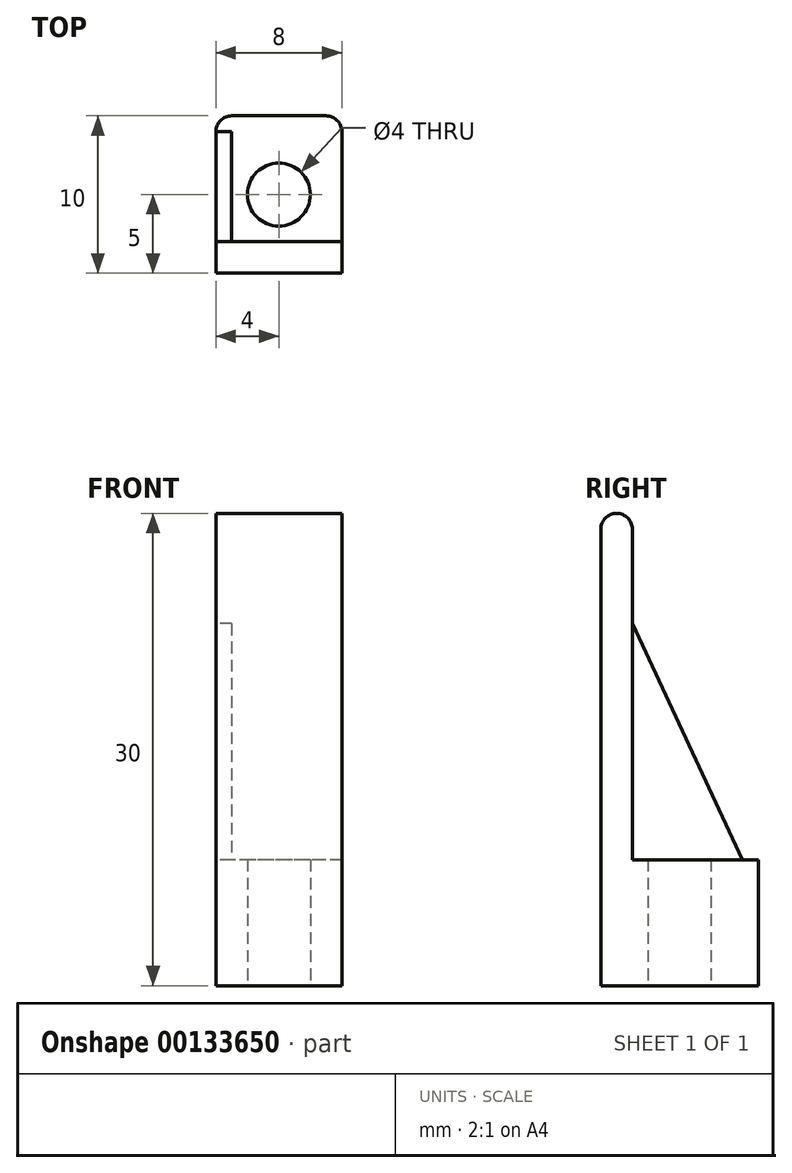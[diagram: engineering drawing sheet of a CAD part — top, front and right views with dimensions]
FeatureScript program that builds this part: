
annotation { "Feature Type Name" : "Feature", "Feature Type Description" : "" }
export const myFeature = defineFeature(function(context is Context, id is Id, definition is map)
    precondition{}
    {
        {
            var Q0;
            Q0=qCreatedBy(makeId("Top.planeOp"),FACE);
            var sketch = newSketch(context, id + "F0", { "sketchPlane" : qUnion([Q0])});
            skLineSegment(sketch, "E0.bottom", {"start": v(3, 5) * mm, "end": v(-3, 5) * mm});
            skLineSegment(sketch, "E0.top", {"start": v(4, -5) * mm, "end": v(-4, -5) * mm});
            skLineSegment(sketch, "E0.left", {"start": v(4, 4) * mm, "end": v(4, -5) * mm});
            skLineSegment(sketch, "E0.right", {"start": v(-4, 4) * mm, "end": v(-4, -5) * mm});
            skPoint(sketch, "E0.middle", {"position": v(0, 0) * mm});
            skCircle(sketch, "E1", {"center": v(0, 0) * mm, "radius": 2 * mm});
            skPoint(sketch, "E2.visualSharp", {"position": v(-4, 5) * mm});
            skArc(sketch, "E2.filletArc", {"start": v(-3, 5) * mm, "mid": v(-3.7, 4.7) * mm, "end": v(-4, 4) * mm});
            skPoint(sketch, "E3.visualSharp", {"position": v(4, 5) * mm});
            skArc(sketch, "E3.filletArc", {"start": v(4, 4) * mm, "mid": v(3.7, 4.7) * mm, "end": v(3, 5) * mm});
            skSolve(sketch);
        }
        {
            var Q0;
            Q0=makeQuery(id+"F0.imprint","IMPRINT",FACE,{"disambiguationData":[TD([[makeQuery(id+"F0.imprint","IMPRINT",EDGE,{"derivedFrom":sQuery(id+"F0.wireOp",EDGE,"E0.bottom")}),1.0]])]});
            extrude(context, id + "F1", {"entities" : qUnion([Q0]), "depth" : 8 * mm});
        }
        {
            var Q0;
            Q0=qCreatedBy(makeId("Top.planeOp"),FACE);
            var sketch = newSketch(context, id + "F2", { "sketchPlane" : qUnion([Q0])});
            skLineSegment(sketch, "E4.bottom", {"start": v(-4, -5) * mm, "end": v(4, -5) * mm});
            skLineSegment(sketch, "E4.top", {"start": v(-4, -3) * mm, "end": v(4, -3) * mm});
            skLineSegment(sketch, "E4.left", {"start": v(-4, -5) * mm, "end": v(-4, -3) * mm});
            skLineSegment(sketch, "E4.right", {"start": v(4, -5) * mm, "end": v(4, -3) * mm});
            skSolve(sketch);
        }
        {
            var Q0;
            Q0=qSketchRegion(id+"F2",true);
            extrude(context, id + "F3", {"entities" : qUnion([Q0]), "operationType" : NewBodyOperationType.ADD, "depth" : 30 * mm});
        }
        {
            var Q0;
            Q0=makeQuery(id+"F3.opExtrude","CAP_EDGE",EDGE,{"disambiguationData":[OSD([sQuery(id+"F2.wireOp",EDGE,"E4.top")])],"isStart":false});
            var Q1;
            Q1=makeQuery(id+"F3.opExtrude","CAP_EDGE",EDGE,{"disambiguationData":[OSD([sQuery(id+"F2.wireOp",EDGE,"E4.bottom")])],"isStart":false});
            fillet(context, id + "F4", {"entities" : qUnion([Q0, Q1]), "radius" : 1 * mm, "tangentPropagation" : true, "allowEdgeOverflow" : false});
        }
        {
            var Q0;
            Q0=makeQuery(id+"F3.boolean.opBoolean","MERGE",FACE,{"derivedFrom":[makeQuery(id+"F1.opExtrude","SWEPT_FACE",FACE,{"disambiguationData":[OSD([sQuery(id+"F0.wireOp",EDGE,"E0.right")])]}),makeQuery(id+"F3.opExtrude","SWEPT_FACE",FACE,{"disambiguationData":[OSD([sQuery(id+"F2.wireOp",EDGE,"E4.left")])]})]});
            var sketch = newSketch(context, id + "F5", { "sketchPlane" : qUnion([Q0])});
            skLineSegment(sketch, "E5", {"start": v(-4, 8) * mm, "end": v(3, 23) * mm});
            skLineSegment(sketch, "E6", {"start": v(3, 23) * mm, "end": v(3, 8) * mm});
            skLineSegment(sketch, "E7", {"start": v(3, 8) * mm, "end": v(-4, 8) * mm});
            skSolve(sketch);
        }
        {
            var Q0;
            Q0=qSketchRegion(id+"F5",true);
            extrude(context, id + "F6", {"entities" : qUnion([Q0]), "operationType" : NewBodyOperationType.ADD, "oppositeDirection" : true, "depth" : 1 * mm});
        }
    });
